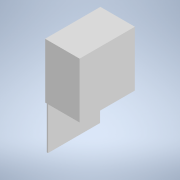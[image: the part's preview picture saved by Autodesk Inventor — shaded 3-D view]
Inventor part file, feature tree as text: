
AUTODESK INVENTOR PART (.ipt)
format: ipt  version: 2022 (Build 260153000, 153)  size: 123,392 bytes
history: native  units: mm
features: extrude x2, sketch x2, other x1
ambient origin geometry x8: Origin, YZ Plane, XZ Plane, XY Plane, X Axis, Y Axis, Z Axis, Center Point
bodies: Body1 (feature_tree)
feature tree (5):
  other  "Твердое тело1"
  extrude  "Выдавливание1"  Depth=14.0mm
  extrude  "Выдавливание2"  Depth=14.0mm
  sketch  "Эскиз1"
  sketch  "Эскиз2"
